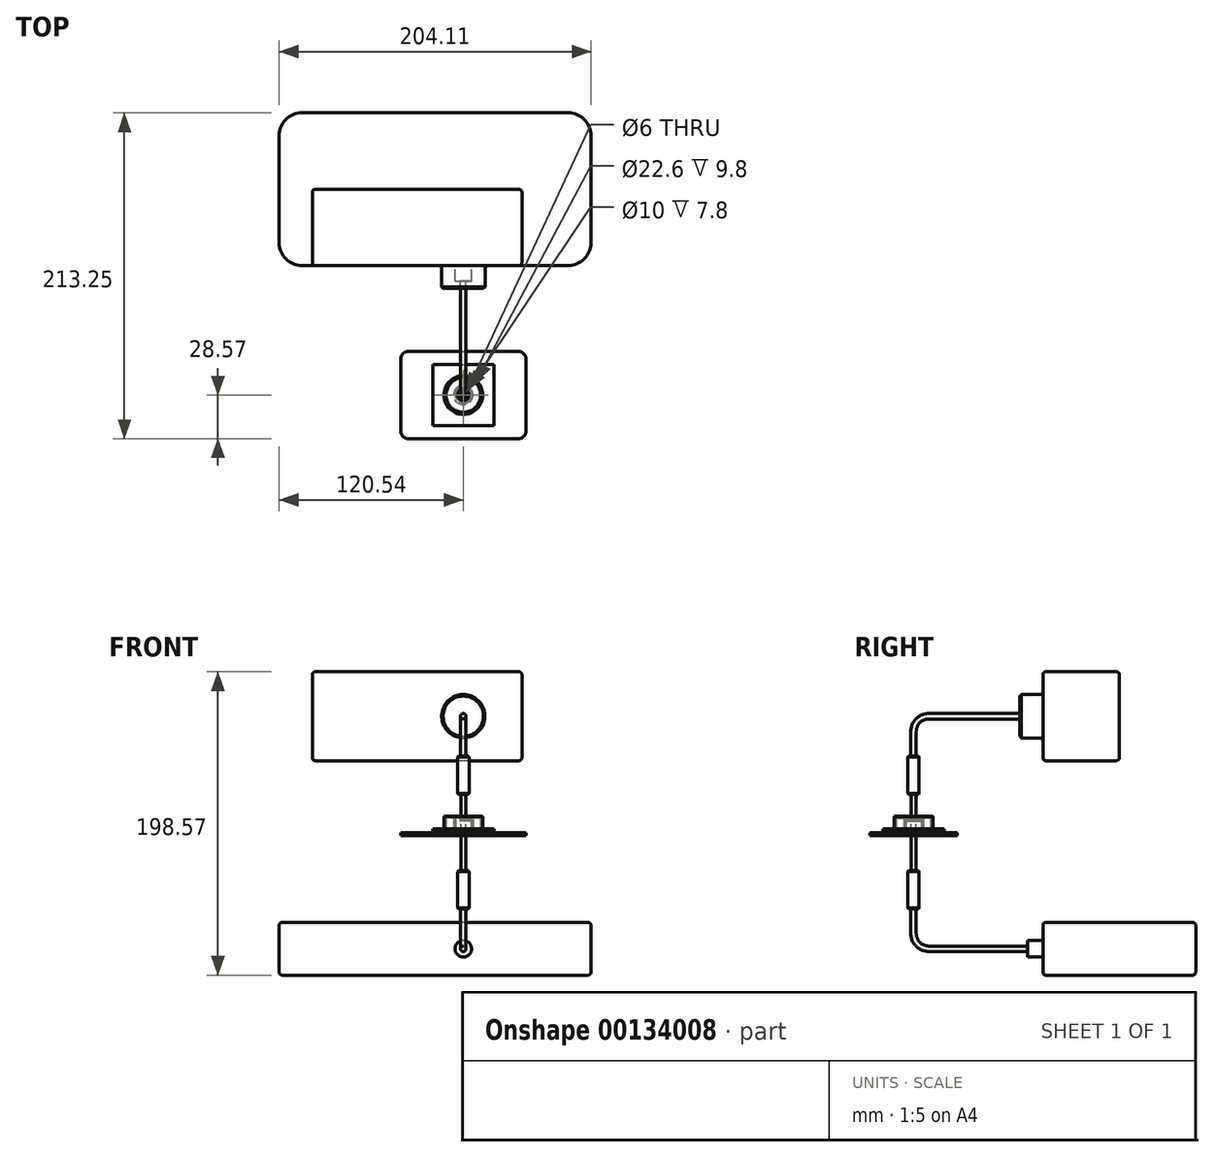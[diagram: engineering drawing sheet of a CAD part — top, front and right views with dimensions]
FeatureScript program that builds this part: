
annotation { "Feature Type Name" : "Feature", "Feature Type Description" : "" }
export const myFeature = defineFeature(function(context is Context, id is Id, definition is map)
    precondition{}
    {
        {
            var Q0;
            Q0=qCreatedBy(makeId("Top.planeOp"),FACE);
            var sketch = newSketch(context, id + "F0", { "sketchPlane" : qUnion([Q0])});
            skLineSegment(sketch, "E0.bottom", {"start": v(-36, 28.57) * mm, "end": v(36, 28.57) * mm});
            skLineSegment(sketch, "E0.top", {"start": v(-36, -28.57) * mm, "end": v(36, -28.57) * mm});
            skLineSegment(sketch, "E0.left", {"start": v(-41, 23.57) * mm, "end": v(-41, -23.57) * mm});
            skLineSegment(sketch, "E0.right", {"start": v(41, 23.57) * mm, "end": v(41, -23.57) * mm});
            skCircle(sketch, "E1", {"center": v(0, 0) * mm, "radius": 3 * mm});
            skPoint(sketch, "E2.visualSharp", {"position": v(-41, 28.57) * mm});
            skArc(sketch, "E2.filletArc", {"start": v(-36, 28.57) * mm, "mid": v(-39.55, 27.1) * mm, "end": v(-41, 23.57) * mm});
            skPoint(sketch, "E3.visualSharp", {"position": v(-41, -28.57) * mm});
            skArc(sketch, "E3.filletArc", {"start": v(-41, -23.57) * mm, "mid": v(-39.55, -27.1) * mm, "end": v(-36, -28.57) * mm});
            skPoint(sketch, "E4.visualSharp", {"position": v(41, -28.57) * mm});
            skArc(sketch, "E4.filletArc", {"start": v(36, -28.57) * mm, "mid": v(39.55, -27.1) * mm, "end": v(41, -23.57) * mm});
            skPoint(sketch, "E5.visualSharp", {"position": v(41, 28.57) * mm});
            skArc(sketch, "E5.filletArc", {"start": v(41, 23.57) * mm, "mid": v(39.55, 27.1) * mm, "end": v(36, 28.57) * mm});
            skSolve(sketch);
        }
        {
            var Q0;
            Q0=makeQuery(id+"F0.imprint","IMPRINT",FACE,{"disambiguationData":[TD([[makeQuery(id+"F0.imprint","IMPRINT",EDGE,{"derivedFrom":sQuery(id+"F0.wireOp",EDGE,"zXq7R44A-xx6G-92k3-GXYH-fsH6qLxIFY6k")}),1.0]])]});
            var Q1;
            Q1=makeQuery(id+"F0.imprint","IMPRINT",FACE,{"disambiguationData":[TD([[makeQuery(id+"F0.imprint","IMPRINT",EDGE,{"derivedFrom":sQuery(id+"F0.wireOp",EDGE,"E0.bottom")}),-1.0]])]});
            extrude(context, id + "F1", {"entities" : qUnion([Q0, Q1]), "oppositeDirection" : true, "depth" : 2 * mm});
        }
        {
            var Q0;
            Q0=makeQuery(id+"F0.imprint","IMPRINT",FACE,{"disambiguationData":[TD([[makeQuery(id+"F0.imprint","IMPRINT",EDGE,{"derivedFrom":sQuery(id+"F0.wireOp",EDGE,"E0.bottom")}),-1.0]])]});
            cPlane(context, id + "F2", {"entities" : qUnion([Q0]), "cplaneType" : CPlaneType.OFFSET, "offset" : 0.5 * mm, "width" : 150 * mm, "height" : 150 * mm});
        }
        {
            var Q0;
            Q0=qCreatedBy(id+"F2.planeOp",FACE);
            var sketch = newSketch(context, id + "F3", { "sketchPlane" : qUnion([Q0])});
            skCircle(sketch, "E6.0", {"center": v(0, 0) * mm, "radius": 3 * mm, "construction": true});
            skCircle(sketch, "E7", {"center": v(0, 0) * mm, "radius": 6.35 * mm});
            skLineSegment(sketch, "E8.bottom", {"start": v(-20, 20) * mm, "end": v(20, 20) * mm});
            skLineSegment(sketch, "E8.top", {"start": v(-20, -20) * mm, "end": v(20, -20) * mm});
            skLineSegment(sketch, "E8.left", {"start": v(-20, 20) * mm, "end": v(-20, -20) * mm});
            skLineSegment(sketch, "E8.right", {"start": v(20, 20) * mm, "end": v(20, -20) * mm});
            skCircle(sketch, "E9", {"center": v(0, 0) * mm, "radius": 12.7 * mm});
            skCircle(sketch, "E10", {"center": v(0, 0) * mm, "radius": 5 * mm});
            skCircle(sketch, "E11", {"center": v(0, 0) * mm, "radius": 11.3 * mm});
            skSolve(sketch);
        }
        {
            var Q0;
            Q0=sQuery(id+"F0.wireOp",VERTEX,"E1.center");
            var Q1;
            Q1=sQuery(id+"F0.wireOp",EDGE,"E0.left");
            cPlane(context, id + "F4", {"entities" : qUnion([Q0, Q1]), "cplaneType" : CPlaneType.LINE_POINT, "offset" : 25 * mm, "width" : 150 * mm, "height" : 150 * mm});
        }
        {
            var Q0;
            Q0=qCreatedBy(id+"F4.planeOp",FACE);
            var sketch = newSketch(context, id + "F5", { "sketchPlane" : qUnion([Q0])});
            skCircle(sketch, "E12", {"center": v(-5, 0.5) * mm, "radius": 0.5 * mm});
            skSolve(sketch);
        }
        {
            var Q0;
            Q0=makeQuery(id+"F5.imprint","IMPRINT",FACE,{"disambiguationData":[TD([[makeQuery(id+"F5.imprint","IMPRINT",EDGE,{"derivedFrom":sQuery(id+"F5.wireOp",EDGE,"E12")}),1.0]])]});
            var Q1;
            Q1=sQuery(id+"F3.wireOp",EDGE,"E7");
            sweep(context, id + "F6", {"profiles" : qUnion([Q0]), "path" : qUnion([Q1])});
        }
        {
            var Q0;
            Q0=makeQuery(id+"F3.imprint","IMPRINT",FACE,{"disambiguationData":[TD([[makeQuery(id+"F3.imprint","IMPRINT",EDGE,{"derivedFrom":sQuery(id+"F3.wireOp",EDGE,"E7")}),-1.0]])]});
            var Q1;
            Q1=makeQuery(id+"F3.imprint","IMPRINT",FACE,{"disambiguationData":[TD([[makeQuery(id+"F3.imprint","IMPRINT",EDGE,{"derivedFrom":sQuery(id+"F3.wireOp",EDGE,"E7")}),1.0]])]});
            var Q2;
            Q2=makeQuery(id+"F3.imprint","IMPRINT",FACE,{"disambiguationData":[TD([[makeQuery(id+"F3.imprint","IMPRINT",EDGE,{"derivedFrom":sQuery(id+"F3.wireOp",EDGE,"E9")}),1.0]])]});
            var Q3;
            Q3=makeQuery(id+"F3.imprint","IMPRINT",FACE,{"disambiguationData":[TD([[makeQuery(id+"F3.imprint","IMPRINT",EDGE,{"derivedFrom":sQuery(id+"F3.wireOp",EDGE,"E8.bottom")}),-1.0]])]});
            var Q4;
            Q4=makeQuery(id+"F3.imprint","IMPRINT",FACE,{"disambiguationData":[TD([[makeQuery(id+"F3.imprint","IMPRINT",EDGE,{"derivedFrom":sQuery(id+"F3.wireOp",EDGE,"E10")}),1.0]])]});
            extrude(context, id + "F7", {"entities" : qUnion([Q0, Q1, Q2, Q3, Q4]), "depth" : 2 * mm});
        }
        {
            var Q0;
            Q0=makeQuery(id+"F3.imprint","IMPRINT",FACE,{"disambiguationData":[TD([[makeQuery(id+"F3.imprint","IMPRINT",EDGE,{"derivedFrom":sQuery(id+"F3.wireOp",EDGE,"E10")}),1.0]])]});
            var Q1;
            Q1=sQuery(id+"F3.wireOp",EDGE,"E7");
            extrude(context, id + "F8", {"entities" : qUnion([Q0]), "surfaceEntities" : qUnion([Q1]), "depth" : 6.9 * mm});
        }
        {
            var Q0;
            Q0=makeQuery(id+"F3.imprint","IMPRINT",FACE,{"disambiguationData":[TD([[makeQuery(id+"F3.imprint","IMPRINT",EDGE,{"derivedFrom":sQuery(id+"F3.wireOp",EDGE,"E7")}),1.0]])]});
            extrude(context, id + "F9", {"entities" : qUnion([Q0]), "depth" : 8 * mm});
        }
        {
            var Q0;
            Q0=makeQuery(id+"F3.imprint","IMPRINT",FACE,{"disambiguationData":[TD([[makeQuery(id+"F3.imprint","IMPRINT",EDGE,{"derivedFrom":sQuery(id+"F3.wireOp",EDGE,"E10")}),1.0]])]});
            var Q1;
            Q1=makeQuery(id+"F3.imprint","IMPRINT",FACE,{"disambiguationData":[TD([[makeQuery(id+"F3.imprint","IMPRINT",EDGE,{"derivedFrom":sQuery(id+"F3.wireOp",EDGE,"E7")}),1.0]])]});
            var Q2;
            Q2=makeQuery(id+"F3.imprint","IMPRINT",FACE,{"disambiguationData":[TD([[makeQuery(id+"F3.imprint","IMPRINT",EDGE,{"derivedFrom":sQuery(id+"F3.wireOp",EDGE,"E7")}),-1.0]])]});
            extrude(context, id + "F10", {"entities" : qUnion([Q0, Q1, Q2]), "depth" : 9 * mm});
        }
        {
            var Q0;
            Q0=makeQuery(id+"F3.imprint","IMPRINT",FACE,{"disambiguationData":[TD([[makeQuery(id+"F3.imprint","IMPRINT",EDGE,{"derivedFrom":sQuery(id+"F3.wireOp",EDGE,"E9")}),1.0]])]});
            extrude(context, id + "F11", {"entities" : qUnion([Q0]), "depth" : 10 * mm});
        }
        {
            var Q0;
            Q0=makeQuery(id+"F9.opExtrude","CAP_FACE",FACE,{"disambiguationData":[OSD([sQuery(id+"F3.wireOp",EDGE,"E7"),sQuery(id+"F3.wireOp",EDGE,"E10")])],"isStart":false});
            var Q1;
            Q1=makeQuery(id+"F11.opExtrude","CAP_FACE",FACE,{"disambiguationData":[OSD([sQuery(id+"F3.wireOp",EDGE,"E9"),sQuery(id+"F3.wireOp",EDGE,"E11")])],"isStart":false});
            chamfer(context, id + "F12", {"entities" : qUnion([Q0, Q1]), "width" : 0.2 * mm, "tangentPropagation" : true});
        }
        {
            var Q0;
            Q0=makeQuery(id+"F0.imprint","IMPRINT",FACE,{"disambiguationData":[TD([[makeQuery(id+"F0.imprint","IMPRINT",EDGE,{"derivedFrom":sQuery(id+"F0.wireOp",EDGE,"E0.bottom")}),-1.0]])]});
            cPlane(context, id + "F13", {"entities" : qUnion([Q0]), "cplaneType" : CPlaneType.OFFSET, "offset" : 25 * mm, "width" : 150 * mm, "height" : 150 * mm});
        }
        {
            var Q0;
            Q0=qCreatedBy(id+"F13.planeOp",FACE);
            var sketch = newSketch(context, id + "F14", { "sketchPlane" : qUnion([Q0])});
            skCircle(sketch, "E13", {"center": v(0, 0) * mm, "radius": 3.7 * mm});
            skCircle(sketch, "E14", {"center": v(0, 0) * mm, "radius": 1.53 * mm});
            skSolve(sketch);
        }
        {
            var Q0;
            Q0=makeQuery(id+"F14.imprint","IMPRINT",FACE,{"disambiguationData":[TD([[makeQuery(id+"F14.imprint","IMPRINT",EDGE,{"derivedFrom":sQuery(id+"F14.wireOp",EDGE,"E13")}),1.0]])]});
            var Q1;
            Q1=makeQuery(id+"F14.imprint","IMPRINT",FACE,{"disambiguationData":[TD([[makeQuery(id+"F14.imprint","IMPRINT",EDGE,{"derivedFrom":sQuery(id+"F14.wireOp",EDGE,"E14")}),1.0]])]});
            var Q2;
            Q2=sQuery(id+"F14.wireOp",EDGE,"E13");
            extrude(context, id + "F15", {"entities" : qUnion([Q0, Q1]), "surfaceEntities" : qUnion([Q2]), "depth" : 25 * mm});
        }
        {
            var Q0;
            Q0=makeQuery(id+"F14.imprint","IMPRINT",FACE,{"disambiguationData":[TD([[makeQuery(id+"F14.imprint","IMPRINT",EDGE,{"derivedFrom":sQuery(id+"F14.wireOp",EDGE,"E14")}),1.0]])]});
            extrude(context, id + "F16", {"entities" : qUnion([Q0]), "oppositeDirection" : true, "depth" : 50 * mm});
        }
        {
            var Q0;
            Q0=makeQuery(id+"F15.opExtrude","SWEPT_FACE",FACE,{"disambiguationData":[OSD([sQuery(id+"F14.wireOp",EDGE,"E13")])]});
            chamfer(context, id + "F17", {"entities" : qUnion([Q0]), "width" : 0.5 * mm, "tangentPropagation" : true});
        }
        {
            var Q0;
            Q0=qCreatedBy(makeId("Right.planeOp"),FACE);
            var sketch = newSketch(context, id + "F18", { "sketchPlane" : qUnion([Q0])});
            skLineSegment(sketch, "E15", {"start": v(-3.7, 25.5) * mm, "end": v(-3.7, 49.5) * mm, "construction": true});
            skLineSegment(sketch, "E16", {"start": v(3.7, 49.5) * mm, "end": v(3.7, 25.5) * mm, "construction": true});
            skLineSegment(sketch, "E17", {"start": v(0, 49.5) * mm, "end": v(0, 66.09) * mm});
            skLineSegment(sketch, "E18", {"start": v(10, 76.09) * mm, "end": v(84.68, 76.09) * mm});
            skPoint(sketch, "E19.visualSharp", {"position": v(0, 76.09) * mm});
            skArc(sketch, "E19.filletArc", {"start": v(10, 76.09) * mm, "mid": v(2.93, 73.16) * mm, "end": v(0, 66.09) * mm});
            skSolve(sketch);
        }
        {
            var Q0;
            Q0=makeQuery(id+"F15.opExtrude","CAP_FACE",FACE,{"disambiguationData":[OSD([sQuery(id+"F14.wireOp",EDGE,"E13")])],"isStart":false});
            var sketch = newSketch(context, id + "F19", { "sketchPlane" : qUnion([Q0])});
            skCircle(sketch, "E20", {"center": v(0, 0) * mm, "radius": 1.78 * mm});
            skSolve(sketch);
        }
        {
            var Q0;
            Q0=makeQuery(id+"F19.imprint","IMPRINT",FACE,{"disambiguationData":[TD([[makeQuery(id+"F19.imprint","IMPRINT",EDGE,{"derivedFrom":sQuery(id+"F19.wireOp",EDGE,"E20")}),1.0]])]});
            var Q1;
            Q1=sQuery(id+"F18.wireOp",EDGE,"E17");
            var Q2;
            Q2=sQuery(id+"F18.wireOp",EDGE,"E19.filletArc");
            var Q3;
            Q3=sQuery(id+"F18.wireOp",EDGE,"E18");
            sweep(context, id + "F20", {"profiles" : qUnion([Q0]), "path" : qUnion([Q1, Q2, Q3])});
        }
        {
            var Q0;
            Q0=makeQuery(id+"F15.opExtrude","SWEPT_BODY",BODY,{"disambiguationData":[OSD([sQuery(id+"F14.wireOp",EDGE,"E13")])]});
            var Q1;
            Q1=makeQuery(id+"F20.opSweep","SWEPT_BODY",BODY,{"disambiguationData":[OSD([sQuery(id+"F18.wireOp",EDGE,"E18"),sQuery(id+"F19.wireOp",EDGE,"E20")])]});
            var Q2;
            Q2=makeQuery(id+"F0.imprint","IMPRINT",FACE,{"disambiguationData":[TD([[makeQuery(id+"F0.imprint","IMPRINT",EDGE,{"derivedFrom":sQuery(id+"F0.wireOp",EDGE,"E0.bottom")}),-1.0]])]});
            mirror(context, id + "F21", {"entities" : qUnion([Q0, Q1]), "mirrorPlane" : qUnion([Q2])});
        }
        {
            var Q0;
            Q0=makeQuery(id+"F20.opSweep","CAP_FACE",FACE,{"disambiguationData":[OSD([sQuery(id+"F18.wireOp",VERTEX,"E18.end"),sQuery(id+"F19.wireOp",EDGE,"E20")])],"isStart":false});
            var sketch = newSketch(context, id + "F22", { "sketchPlane" : qUnion([Q0])});
            skCircle(sketch, "E21.0", {"center": v(0, 76.09) * mm, "radius": 1.78 * mm, "construction": true});
            skCircle(sketch, "E22.0", {"center": v(0, -76.09) * mm, "radius": 1.78 * mm, "construction": true});
            skLineSegment(sketch, "E23.bottom", {"start": v(-38.34, 105.2) * mm, "end": v(98.82, 105.2) * mm});
            skLineSegment(sketch, "E23.top", {"start": v(-38.34, 46.97) * mm, "end": v(98.82, 46.97) * mm});
            skLineSegment(sketch, "E23.left", {"start": v(-38.34, 105.2) * mm, "end": v(-38.34, 46.97) * mm});
            skLineSegment(sketch, "E23.right", {"start": v(98.82, 105.2) * mm, "end": v(98.82, 46.97) * mm});
            skLineSegment(sketch, "E24.bottom", {"start": v(-83.57, -58.81) * mm, "end": v(120.54, -58.81) * mm});
            skLineSegment(sketch, "E24.top", {"start": v(-83.57, -93.36) * mm, "end": v(120.54, -93.36) * mm});
            skLineSegment(sketch, "E24.left", {"start": v(-83.57, -58.81) * mm, "end": v(-83.57, -93.36) * mm});
            skLineSegment(sketch, "E24.right", {"start": v(120.54, -58.81) * mm, "end": v(120.54, -93.36) * mm});
            skCircle(sketch, "E25", {"center": v(0, 76.09) * mm, "radius": 14.18 * mm});
            skCircle(sketch, "E26", {"center": v(0, -76.09) * mm, "radius": 5.39 * mm});
            skPoint(sketch, "E27", {"position": v(-83.57, -76.09) * mm});
            skPoint(sketch, "E28", {"position": v(-38.34, 76.09) * mm});
            skSolve(sketch);
        }
        {
            var Q0;
            Q0=makeQuery(id+"F22.imprint","IMPRINT",FACE,{"disambiguationData":[TD([[makeQuery(id+"F22.imprint","IMPRINT",EDGE,{"derivedFrom":sQuery(id+"F22.wireOp",EDGE,"E23.bottom")}),-1.0]])]});
            var Q1;
            Q1=makeQuery(id+"F22.imprint","IMPRINT",FACE,{"disambiguationData":[TD([[makeQuery(id+"F22.imprint","IMPRINT",EDGE,{"derivedFrom":sQuery(id+"F22.wireOp",EDGE,"E25")}),1.0]])]});
            var Q2;
            Q2=makeQuery(id+"F22.imprint","IMPRINT",FACE,{"disambiguationData":[TD([[makeQuery(id+"F22.imprint","IMPRINT",EDGE,{"derivedFrom":makeQuery(id+"F20.opSweep","CAP_EDGE",EDGE,{"disambiguationData":[OSD([sQuery(id+"F18.wireOp",VERTEX,"E18.end"),sQuery(id+"F19.wireOp",EDGE,"E20")])],"isStart":false})}),1.0]])]});
            extrude(context, id + "F23", {"entities" : qUnion([Q0, Q1, Q2]), "depth" : 50 * mm});
        }
        {
            var Q0;
            Q0=makeQuery(id+"F22.imprint","IMPRINT",FACE,{"disambiguationData":[TD([[makeQuery(id+"F22.imprint","IMPRINT",EDGE,{"derivedFrom":sQuery(id+"F22.wireOp",EDGE,"E25")}),1.0]])]});
            extrude(context, id + "F24", {"entities" : qUnion([Q0]), "operationType" : NewBodyOperationType.ADD, "oppositeDirection" : true, "depth" : 15 * mm});
        }
        {
            var Q0;
            Q0=makeQuery(id+"F22.imprint","IMPRINT",FACE,{"disambiguationData":[TD([[makeQuery(id+"F22.imprint","IMPRINT",EDGE,{"derivedFrom":sQuery(id+"F22.wireOp",EDGE,"E24.bottom")}),-1.0]])]});
            var Q1;
            Q1=makeQuery(id+"F22.imprint","IMPRINT",FACE,{"disambiguationData":[TD([[makeQuery(id+"F22.imprint","IMPRINT",EDGE,{"derivedFrom":sQuery(id+"F22.wireOp",EDGE,"E26")}),1.0]])]});
            extrude(context, id + "F25", {"entities" : qUnion([Q0, Q1]), "depth" : 100 * mm});
        }
        {
            var Q0;
            Q0=makeQuery(id+"F22.imprint","IMPRINT",FACE,{"disambiguationData":[TD([[makeQuery(id+"F22.imprint","IMPRINT",EDGE,{"derivedFrom":sQuery(id+"F22.wireOp",EDGE,"E26")}),1.0]])]});
            var Q1;
            Q1=sQuery(id+"F22.wireOp",EDGE,"E26");
            extrude(context, id + "F26", {"entities" : qUnion([Q0]), "operationType" : NewBodyOperationType.ADD, "surfaceEntities" : qUnion([Q1]), "oppositeDirection" : true, "depth" : 10 * mm});
        }
        {
            var Q0;
            Q0=makeQuery(id+"F25.opExtrude","CAP_EDGE",EDGE,{"disambiguationData":[OSD([sQuery(id+"F22.wireOp",EDGE,"E24.left")])],"isStart":false});
            var Q1;
            Q1=makeQuery(id+"F25.opExtrude","CAP_EDGE",EDGE,{"disambiguationData":[OSD([sQuery(id+"F22.wireOp",EDGE,"E24.right")])],"isStart":false});
            var Q2;
            Q2=makeQuery(id+"F25.opExtrude","CAP_EDGE",EDGE,{"disambiguationData":[OSD([sQuery(id+"F22.wireOp",EDGE,"E24.right")])],"isStart":true});
            var Q3;
            Q3=makeQuery(id+"F25.opExtrude","CAP_EDGE",EDGE,{"disambiguationData":[OSD([sQuery(id+"F22.wireOp",EDGE,"E24.left")])],"isStart":true});
            fillet(context, id + "F27", {"entities" : qUnion([Q0, Q1, Q2, Q3]), "radius" : 15 * mm, "tangentPropagation" : true, "allowEdgeOverflow" : false});
        }
        {
            var Q0;
            Q0=makeQuery(id+"F25.opExtrude","SWEPT_FACE",FACE,{"disambiguationData":[OSD([sQuery(id+"F22.wireOp",EDGE,"E24.bottom")])]});
            var Q1;
            Q1=makeQuery(id+"F25.opExtrude","SWEPT_FACE",FACE,{"disambiguationData":[OSD([sQuery(id+"F22.wireOp",EDGE,"E24.top")])]});
            var Q2;
            {var subQ0=sQuery(id+"F22.wireOp",EDGE,"E23.right");var subQ1=sQuery(id+"F22.wireOp",EDGE,"E23.bottom");var subQ2=sQuery(id+"F22.wireOp",EDGE,"E23.top");var subQ3=sQuery(id+"F22.wireOp",EDGE,"E23.left");Q2=makeQuery(id+"F24.boolean.opBoolean","SPLIT",FACE,{"disambiguationData":[TD([makeQuery(id+"F23.opExtrude","SWEPT_FACE",FACE,{"disambiguationData":[OSD([subQ1])]})])],"derivedFrom":makeQuery(id+"F23.opExtrude","CAP_FACE",FACE,{"disambiguationData":[OSD([subQ1,subQ2,subQ3,subQ0])],"isStart":true})});}
            var Q3;
            Q3=makeQuery(id+"F23.opExtrude","CAP_FACE",FACE,{"disambiguationData":[OSD([sQuery(id+"F22.wireOp",EDGE,"E23.bottom"),sQuery(id+"F22.wireOp",EDGE,"E23.top"),sQuery(id+"F22.wireOp",EDGE,"E23.left"),sQuery(id+"F22.wireOp",EDGE,"E23.right")])],"isStart":false});
            var Q4;
            Q4=makeQuery(id+"F23.opExtrude","SWEPT_FACE",FACE,{"disambiguationData":[OSD([sQuery(id+"F22.wireOp",EDGE,"E23.left")])]});
            var Q5;
            Q5=makeQuery(id+"F23.opExtrude","SWEPT_FACE",FACE,{"disambiguationData":[OSD([sQuery(id+"F22.wireOp",EDGE,"E23.right")])]});
            fillet(context, id + "F28", {"entities" : qUnion([Q0, Q1, Q2, Q3, Q4, Q5]), "radius" : 2 * mm, "tangentPropagation" : true, "allowEdgeOverflow" : false});
        }
        {
            var Q0;
            Q0=makeQuery(id+"F24.opExtrude","CAP_EDGE",EDGE,{"disambiguationData":[OSD([sQuery(id+"F22.wireOp",EDGE,"E25")])],"isStart":false});
            chamfer(context, id + "F29", {"entities" : qUnion([Q0]), "width" : 1 * mm, "tangentPropagation" : true});
        }
    });
